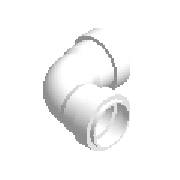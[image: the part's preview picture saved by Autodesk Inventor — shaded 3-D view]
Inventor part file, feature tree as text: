
AUTODESK INVENTOR PART (.ipt)
format: ipt  version: 2023.1 (Build 271208000, 208)  size: 283,648 bytes
history: native  units: mm (DEFAULTED — no unit token found)
features: other x4, sketch x3, revolve x1
ambient origin geometry x8: Origin, YZ Plane, XZ Plane, XY Plane, X Axis, Y Axis, Z Axis, Center Point
bodies: Solid1 (feature_tree)
feature tree (8):
  sketch  "Sketch1"  dims[d3=90.0deg d0=2.4mm]
  revolve  "Revolution1"  [1 undecoded]
  sketch  "Sketch2"  dims[d1=2.4mm]
  other  "Work Axis31"
  other  "Work Point21"
  other  "Work Axis32"
  other  "Work Point22"
  sketch  "Sketch3"  dims[d2=2.4mm d4=2.88mm d5=2.4mm d6=7.2mm d7=160.5mm d8=32.0mm d9=42.0mm d10=0.0mm d11=11.2mm d12=160.0mm d13=3.2mm d14=2.88mm d15=90.0mm d16=90.0mm d17=160.5mm d18=2.4mm d19=2.4mm d20=2.4mm d21=2.4mm d22=4.8mm d23=2.88mm d24=3.2mm d25=160.0mm d26=11.2mm d27=32.0mm d28=42.0mm d29=90.0mm d30=90.0mm d31=2.88mm d206=90.0deg d207=0.0mm]
note: 1 required parameter value undecoded (feature->parameter linkage not recoverable at this tier; creation-order binding heuristic only, values carry confidence <= 0.55)
